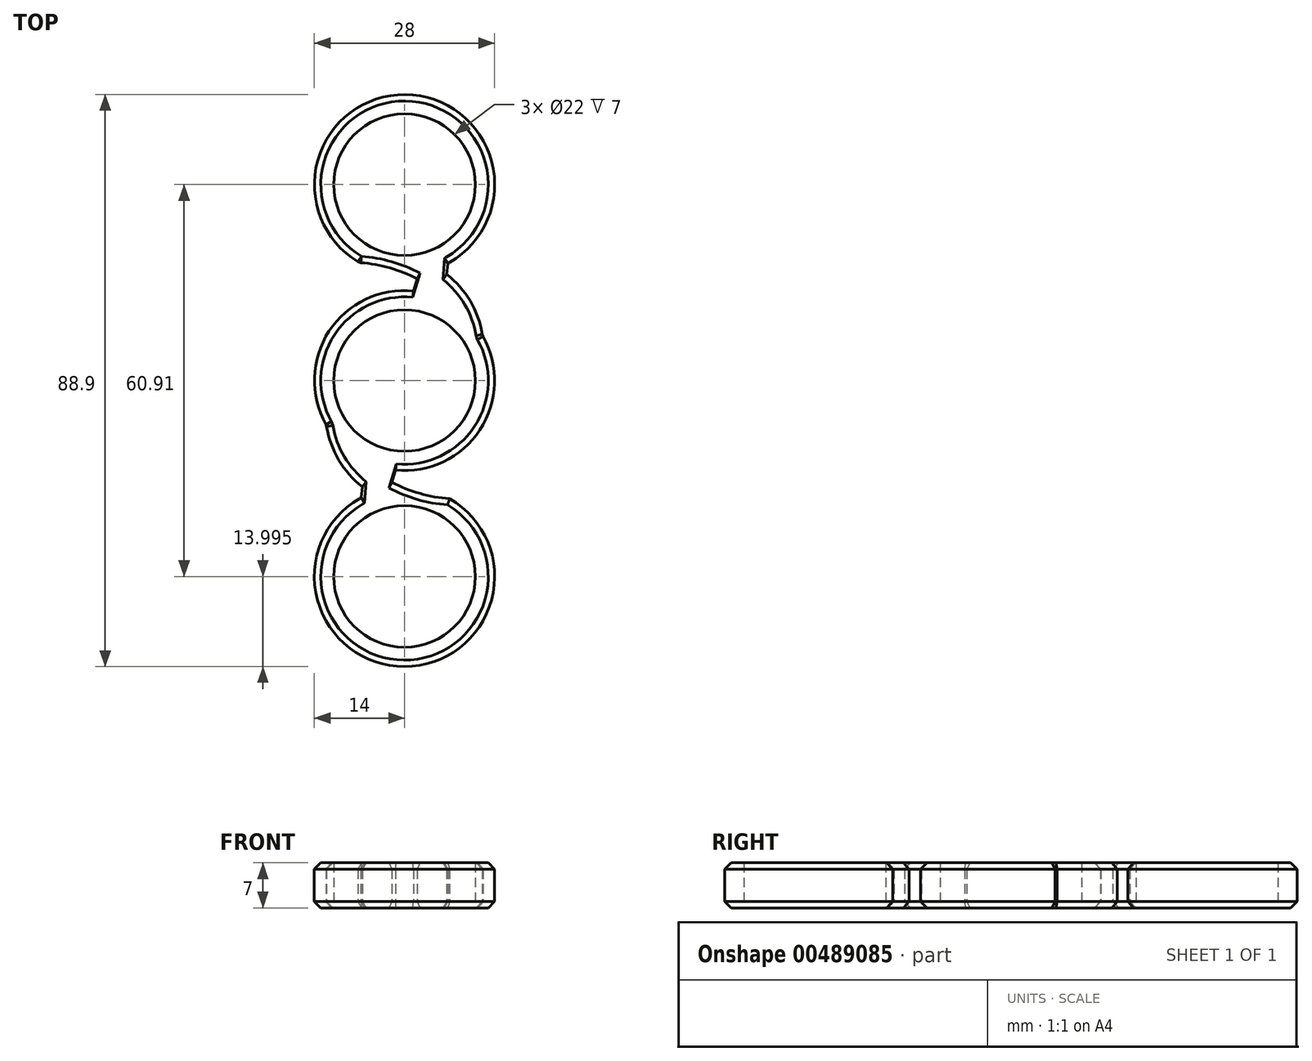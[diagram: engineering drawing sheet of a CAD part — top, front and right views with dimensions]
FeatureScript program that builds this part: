
annotation { "Feature Type Name" : "Feature", "Feature Type Description" : "" }
export const myFeature = defineFeature(function(context is Context, id is Id, definition is map)
    precondition{}
    {
        {
            var Q0;
            Q0=qCreatedBy(makeId("Top.planeOp"),FACE);
            var sketch = newSketch(context, id + "F0", { "sketchPlane" : qUnion([Q0])});
            skCircle(sketch, "E0", {"center": v(0, 0) * mm, "radius": 11 * mm});
            skArc(sketch, "E1.0", {"start": v(7, 12.12) * mm, "mid": v(-9.9, 9.9) * mm, "end": v(-12.12, -7) * mm});
            skCircle(sketch, "E2", {"center": v(0, 30.45) * mm, "radius": 11 * mm});
            skArc(sketch, "E3.0", {"start": v(7, 18.33) * mm, "mid": v(0, 44.45) * mm, "end": v(-7, 18.33) * mm});
            skLineSegment(sketch, "E4", {"start": v(0, 30.45) * mm, "end": v(-5.5, 20.93) * mm});
            skLineSegment(sketch, "E5", {"start": v(0, 19.45) * mm, "end": v(0, 30.45) * mm});
            skLineSegment(sketch, "E6.MirrorCS", {"start": v(0, 30.45) * mm, "end": v(5.5, 20.93) * mm});
            skLineSegment(sketch, "E7", {"start": v(0, 19.45) * mm, "end": v(0, 16.73) * mm});
            skPoint(sketch, "E8", {"position": v(0, 16.73) * mm});
            skLineSegment(sketch, "E9", {"start": v(0, 0) * mm, "end": v(7, 12.12) * mm});
            skArc(sketch, "E10", {"start": v(7, 12.12) * mm, "mid": v(0.56, 16.49) * mm, "end": v(-7, 18.33) * mm});
            skLineSegment(sketch, "E11", {"start": v(0, 0) * mm, "end": v(12.12, 7) * mm});
            skArc(sketch, "E12", {"start": v(12.12, 7) * mm, "mid": v(9.8, 13) * mm, "end": v(5.17, 17.47) * mm});
            skArc(sketch, "E13", {"start": v(7, 18.33) * mm, "mid": v(6.1, 17.86) * mm, "end": v(5.17, 17.47) * mm});
            skPoint(sketch, "E14.orphan", {"position": v(0, 14) * mm});
            skArc(sketch, "E15.MirrorCS", {"start": v(7, -18.33) * mm, "mid": v(0, -44.45) * mm, "end": v(-7, -18.33) * mm});
            skCircle(sketch, "E16.MirrorC", {"center": v(0, -30.45) * mm, "radius": 11 * mm});
            skArc(sketch, "E17.MirrorCS", {"start": v(-7, -18.33) * mm, "mid": v(0, -44.45) * mm, "end": v(7, -18.33) * mm});
            skArc(sketch, "E18.MirrorCS", {"start": v(-12.12, -7) * mm, "mid": v(-9.8, -13) * mm, "end": v(-5.17, -17.47) * mm});
            skArc(sketch, "E19.MirrorCS", {"start": v(-7, -12.12) * mm, "mid": v(-0.56, -16.49) * mm, "end": v(7, -18.33) * mm});
            skArc(sketch, "E20.MirrorCS", {"start": v(-7, -18.33) * mm, "mid": v(-6.1, -17.86) * mm, "end": v(-5.17, -17.47) * mm});
            skPoint(sketch, "E21.MirrorCS.end.orphan", {"position": v(5.17, -17.47) * mm});
            skPoint(sketch, "E21.MirrorCS.start.orphan", {"position": v(12.12, -7) * mm});
            skPoint(sketch, "E22.orphan", {"position": v(7, -12.12) * mm});
            skPoint(sketch, "E23.MirrorCS.start.orphan", {"position": v(7, -18.33) * mm});
            skPoint(sketch, "E24.MirrorCS.end.orphan", {"position": v(-7, -18.33) * mm});
            skArc(sketch, "E25.trimOffspring", {"start": v(-7, -12.12) * mm, "mid": v(9.9, -9.9) * mm, "end": v(12.12, 7) * mm});
            skSolve(sketch);
        }
        {
            var Q0;
            {var subQ4=sQuery(id+"F0.wireOp",EDGE,"E1.0");Q0=makeQuery(id+"F0.imprint","IMPRINT",FACE,{"disambiguationData":[TD([[makeQuery(id+"F0.imprint","IMPRINT",EDGE,{"derivedFrom":subQ4}),1.0]])]});}
            var Q1;
            {var subQ1=sQuery(id+"F0.wireOp",EDGE,"E3.0");Q1=makeQuery(id+"F0.imprint","IMPRINT",FACE,{"disambiguationData":[TD([[makeQuery(id+"F0.imprint","IMPRINT",EDGE,{"derivedFrom":subQ1}),1.0]])]});}
            extrude(context, id + "F1", {"entities" : qUnion([Q0, Q1]), "endBound" : BoundingType.SYMMETRIC, "depth" : 7 * mm});
        }
        {
            var Q0;
            Q0=makeQuery(id+"F1.opExtrude","SWEPT_FACE",FACE,{"disambiguationData":[OSD([sQuery(id+"F0.wireOp",EDGE,"E17.MirrorCS")])]});
            var Q1;
            Q1=makeQuery(id+"F1.opExtrude","SWEPT_FACE",FACE,{"disambiguationData":[OSD([sQuery(id+"F0.wireOp",EDGE,"E25.trimOffspring")])]});
            var Q2;
            Q2=makeQuery(id+"F1.opExtrude","SWEPT_FACE",FACE,{"disambiguationData":[OSD([sQuery(id+"F0.wireOp",EDGE,"E12")])]});
            var Q3;
            Q3=makeQuery(id+"F1.opExtrude","SWEPT_FACE",FACE,{"disambiguationData":[OSD([sQuery(id+"F0.wireOp",EDGE,"E3.0")])]});
            var Q4;
            Q4=makeQuery(id+"F1.opExtrude","SWEPT_FACE",FACE,{"disambiguationData":[OSD([sQuery(id+"F0.wireOp",EDGE,"E1.0")])]});
            var Q5;
            Q5=makeQuery(id+"F1.opExtrude","SWEPT_FACE",FACE,{"disambiguationData":[OSD([sQuery(id+"F0.wireOp",EDGE,"E18.MirrorCS")])]});
            chamfer(context, id + "F2", {"entities" : qUnion([Q0, Q1, Q2, Q3, Q4, Q5]), "width" : 1 * mm, "tangentPropagation" : true});
        }
    });
